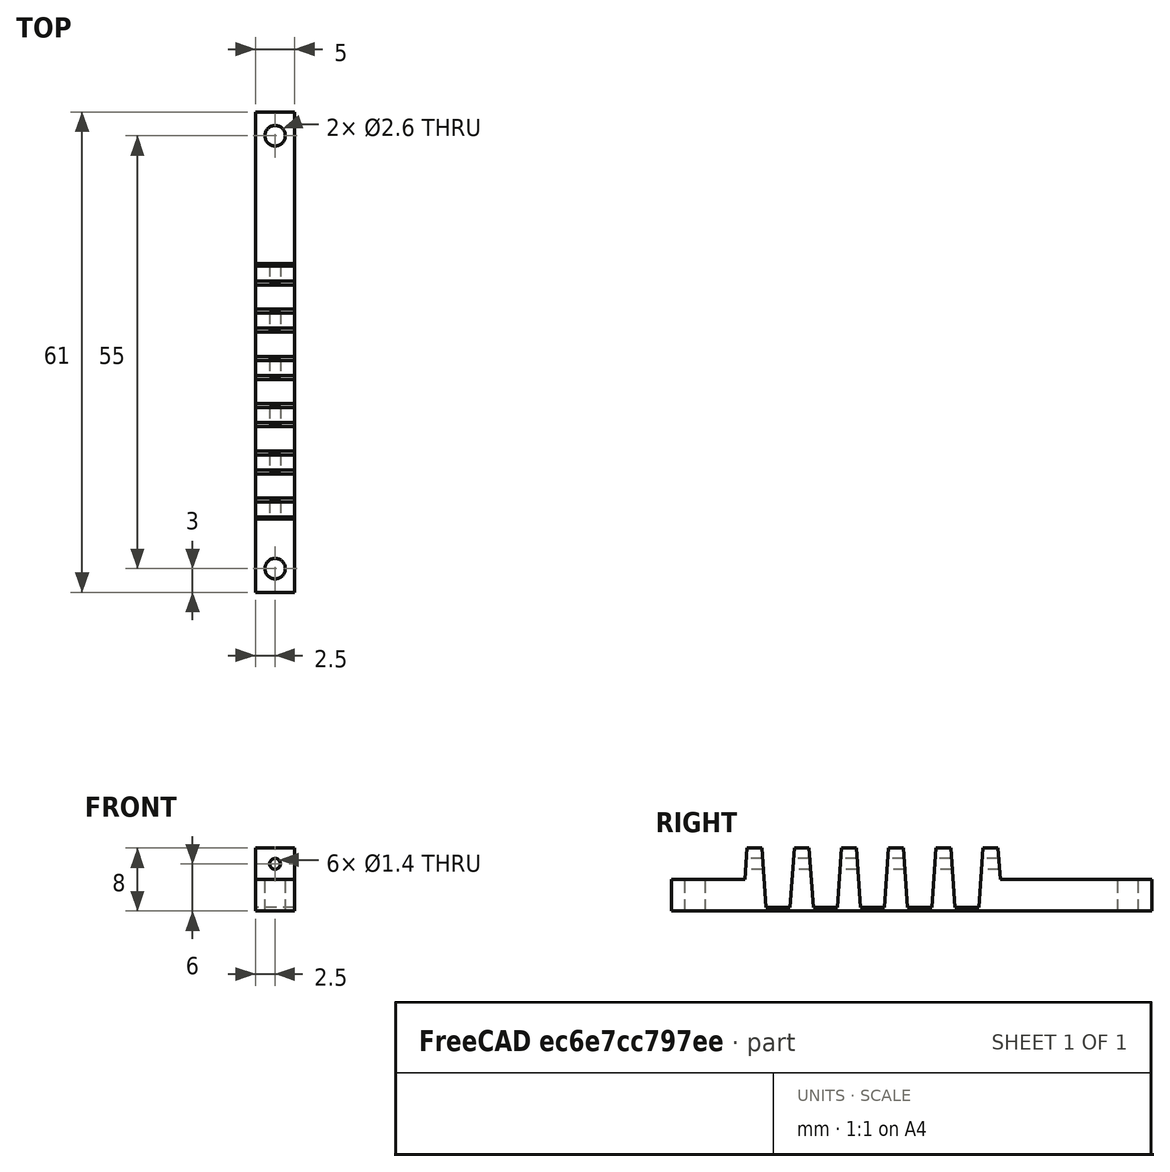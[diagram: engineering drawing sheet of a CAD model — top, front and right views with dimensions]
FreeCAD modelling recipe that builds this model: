
FCSTD DOCUMENT  (FreeCAD 0.18.4R)
Label: flex1
License: All rights reserved
LicenseURL: http://en.wikipedia.org/wiki/All_rights_reserved
objects: Part::Box×6, Part::Feature×5, Part::MultiFuse×3, Part::Cylinder×3, Part::Cut×2
note: 19 computed .brp shape members not serialized (recipe doc carries the construction recipe); baked Part::Feature solids carry a one-line shape summary decoded from their .brp

FEATURE [Part::Box] Box  label="Cube"
  AttacherType = Attacher::AttachEngine3D
  Height = 0.5
  Length = 5
  Placement = pos=(0,10,0) rot=(0,0,1;0rad)
  Width = 33
FEATURE [Part::Box] Box001  label="Cube001"
  AttacherType = Attacher::AttachEngine3D
  Height = 8
  Length = 5
  Width = 3
FEATURE [Part::Box] Box002  label="Cube002"
  AttacherType = Attacher::AttachEngine3D
  Height = 10
  Length = 7
  Placement = pos=(-1,-3.06245,-0.788295) rot=(1,0,0;6.21337rad)
  Width = 3
FEATURE [Part::Box] Box003  label="Cube003"
  AttacherType = Attacher::AttachEngine3D
  Height = 10
  Length = 7
  Placement = pos=(-1,3.06245,-0.788295) rot=(1,0,0;0.069813rad)
  Width = 3
FEATURE [Part::MultiFuse] Fusion
  Shapes = -> [Box003,Box002]
FEATURE [Part::Cut] Cut
  Base = -> Box001
  Placement = pos=(0,10,0) rot=(0,0,1;0rad)
  Tool = -> Fusion
FEATURE [Part::Feature] Cut001 .. Cut005  x5 (patterned run collapsed; names and placements below)
  shape: bbox 5 x 3 x 8 mm, 7 faces (baked)
  placements: 5 in arithmetic series — first pos=(0,16,0) rot=(0,0,1;0rad), step (0,6,0), last pos=(0,40,0) rot=(0,0,1;0rad)
FEATURE [Part::Box] Box004  label="Cube004"
  AttacherType = Attacher::AttachEngine3D
  Height = 4
  Length = 5
  Placement = pos=(0,1,0) rot=(0,0,1;0rad)
  Width = 10
FEATURE [Part::Box] Box005  label="Cube005"
  AttacherType = Attacher::AttachEngine3D
  Height = 4
  Length = 5
  Placement = pos=(0,42,0) rot=(0,0,1;0rad)
  Width = 20
FEATURE [Part::Cylinder] Cylinder
  Angle = 360
  AttacherType = Attacher::AttachEngine3D
  Height = 10
  Placement = pos=(2.5,4,-1) rot=(0,0,1;0rad)
  Radius = 1.3
FEATURE [Part::Cylinder] Cylinder001
  Angle = 360
  AttacherType = Attacher::AttachEngine3D
  Height = 100
  Placement = pos=(2.5,59,6) rot=(1,0,0;1.5708rad)
  Radius = 0.7
FEATURE [Part::Cylinder] Cylinder002
  Angle = 360
  AttacherType = Attacher::AttachEngine3D
  Height = 10
  Placement = pos=(2.5,59,-1) rot=(0,0,1;0rad)
  Radius = 1.3
FEATURE [Part::MultiFuse] Fusion001
  Shapes = -> [Box005,Cut002,Cut005,Box,Box004,Cut001,Cut003,Cut,Cut004]
FEATURE [Part::MultiFuse] Fusion002
  Shapes = -> [Cylinder,Cylinder001,Cylinder002]
FEATURE [Part::Cut] Cut006
  Base = -> Fusion001
  Tool = -> Fusion002
